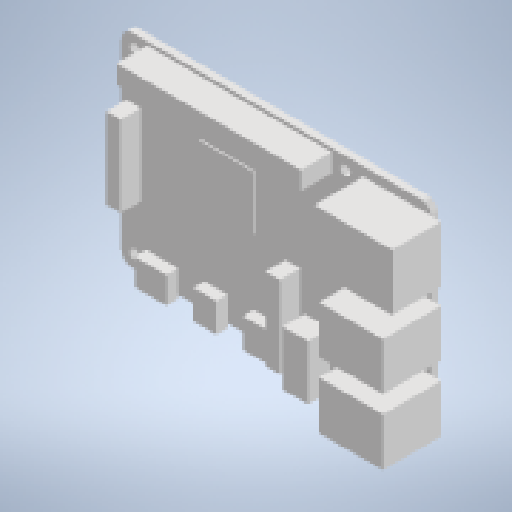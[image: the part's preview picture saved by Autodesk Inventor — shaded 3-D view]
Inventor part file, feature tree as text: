
AUTODESK INVENTOR PART (.ipt)
format: ipt  version: 2023 (Build 270158000, 158)  size: 519,680 bytes
history: native  units: in
note: dims shown in document units (in); Inventor stores cm internally (conversion verified against a paired STEP export)
features: extrude x13, sketch x4, fillet x1, hole x1, other x1
ambient origin geometry x8: Origin, YZ Plane, XZ Plane, XY Plane, X Axis, Y Axis, Z Axis, Center Point
bodies: Solid1 (feature_tree)
feature tree (20):
  extrude  "Extrusion1"  Depth=2.2047in
  fillet  "Fillet1"  Radius=0.0787in
  hole  "Hole1"  [1 undecoded]
  sketch  "Sketch3"  dims[d6=0.1378in d7=2.2835in]
  extrude  "Extrusion2"  Depth=0.1378in
  extrude  "Extrusion3"  Depth=0.2756in
  extrude  "Extrusion4"  Depth=1.998in
  extrude  "Extrusion5"  Depth=0.1969in
  extrude  "Extrusion6"  Depth=0.0394in
  extrude  "Extrusion7"  Depth=0.6594in
  extrude  "Extrusion8"  Depth=0.876in
  extrude  "Extrusion9"  Depth=0.1575in
  extrude  "Extrusion10"  Depth=0.0492in
  extrude  "Extrusion11"  Depth=0.0394in
  extrude  "Extrusion12"  Depth=0.0492in
  extrude  "Extrusion13"  Depth=0.2854in
  sketch  "Sketch1"  dims[d0=3.3465in d1=2.2047in d2=0.0787in d3=0.0in]
  sketch  "Sketch2"  dims[d4=0.1181in d5=0.1378in]
  other  "Image1"
  sketch  "Sketch4"  dims[d8=0.1378in d9=0.1063in d10=0.2362in d11=0.1575in d12=0.0787in d13=90.0deg d14=0.315in d15=0.8108in d55=0.2756in d56=1.998in d57=0.1969in d58=0.0394in d59=0.6594in d60=0.876in d61=0.1575in d62=0.0492in d63=0.0394in d64=0.0492in d65=0.2854in d66=0.3445in d67=0.2657in d68=0.8957in d69=0.2461in d70=0.2657in d71=1.4272in d72=0.2461in d73=0.1575in d74=0.8858in d75=1.7717in d76=0.0197in d77=0.2756in d78=0.0886in d79=1.0925in d80=0.5906in d81=0.3543in d82=0.6929in d83=0.5217in d84=0.1102in d85=0.5118in d86=1.063in d87=0.8425in d88=0.6102in d89=1.8012in d90=0.5906in d91=0.5906in d92=0.6299in d93=0.8504in d94=0.2165in d95=0.0in d96=0.3346in d97=0.0in d98=0.0945in d99=0.0in d100=0.126in d101=0.0in d102=0.1181in d103=0.0in d104=0.1181in d105=0.0in d106=0.2165in d107=0.0in d108=0.2362in d109=0.0in d110=0.6299in d111=0.0in d112=0.6299in d113=0.0in d114=0.5315in d115=0.0in d117=0.0787in d118=0.0in]
note: 1 required parameter value undecoded (feature->parameter linkage not recoverable at this tier; creation-order binding heuristic only, values carry confidence <= 0.55)
